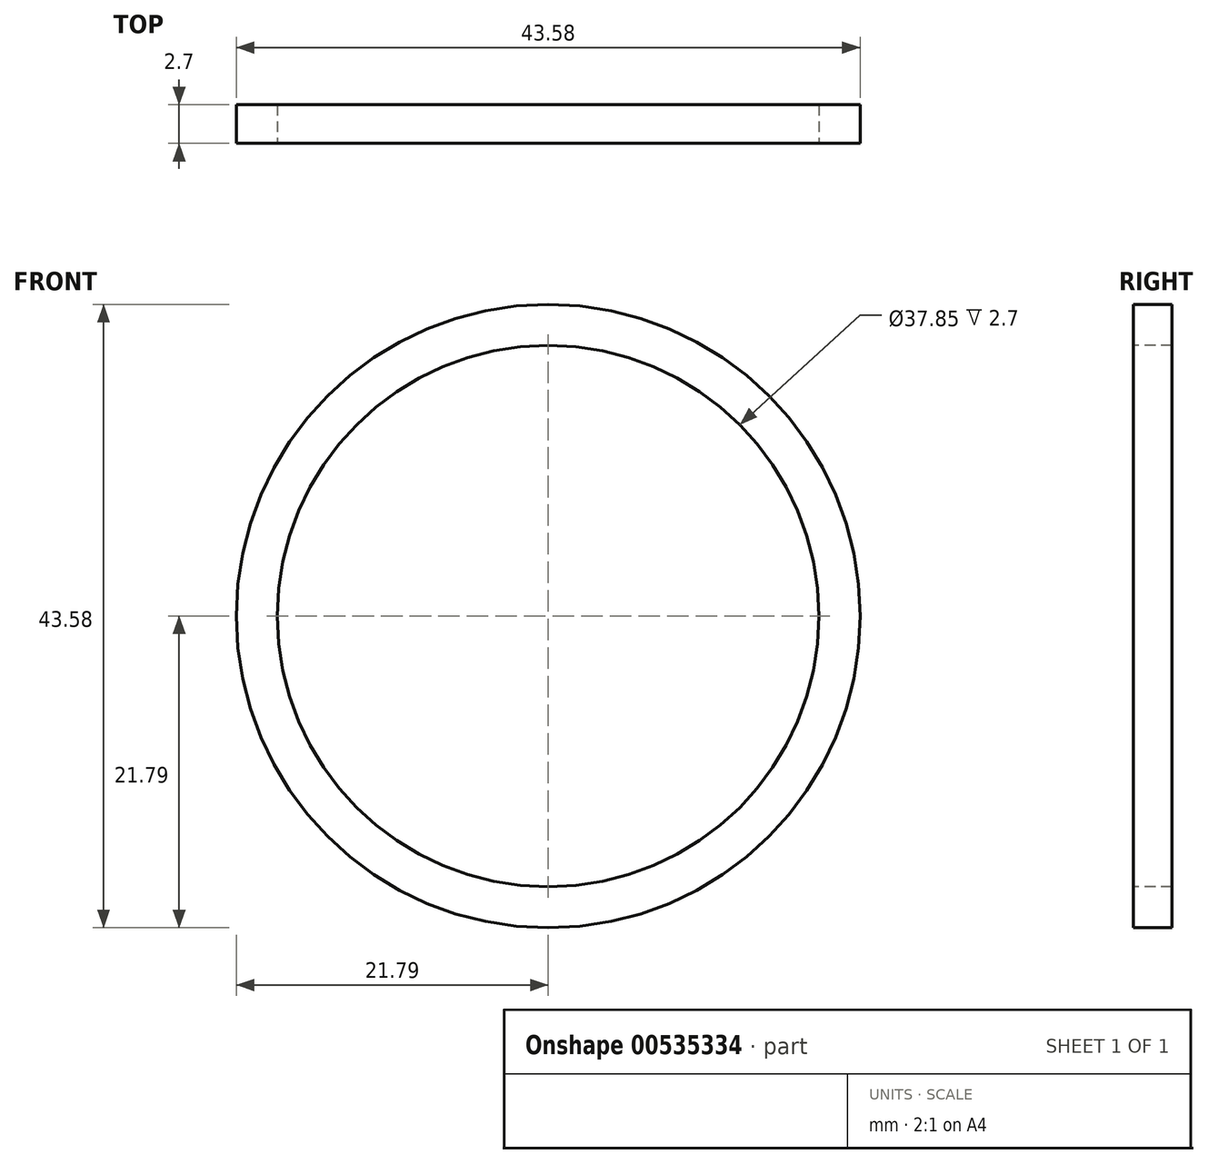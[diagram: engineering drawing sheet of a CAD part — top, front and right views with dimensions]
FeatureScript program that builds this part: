
annotation { "Feature Type Name" : "Feature", "Feature Type Description" : "" }
export const myFeature = defineFeature(function(context is Context, id is Id, definition is map)
    precondition{}
    {
        {
            var Q0;
            Q0=qCreatedBy(makeId("Front.planeOp"),FACE);
            var sketch = newSketch(context, id + "F0", { "sketchPlane" : qUnion([Q0])});
            skCircle(sketch, "E0", {"center": v(0, 0) * mm, "radius": 6.06 * mm});
            skCircle(sketch, "E1", {"center": v(0, 0) * mm, "radius": 10.13 * mm});
            skCircle(sketch, "E2", {"center": v(0, 0) * mm, "radius": 18.92 * mm});
            skCircle(sketch, "E3", {"center": v(0, 0) * mm, "radius": 21.8 * mm});
            skSolve(sketch);
        }
        {
            var Q0;
            Q0=makeQuery(id+"F0.imprint","IMPRINT",FACE,{"disambiguationData":[TD([[makeQuery(id+"F0.imprint","IMPRINT",EDGE,{"derivedFrom":sQuery(id+"F0.wireOp",EDGE,"E2")}),-1.0]])]});
            extrude(context, id + "F1", {"entities" : qUnion([Q0]), "oppositeDirection" : true, "depth" : 2.7 * mm, "offsetDistance" : 25 * mm});
        }
    });
